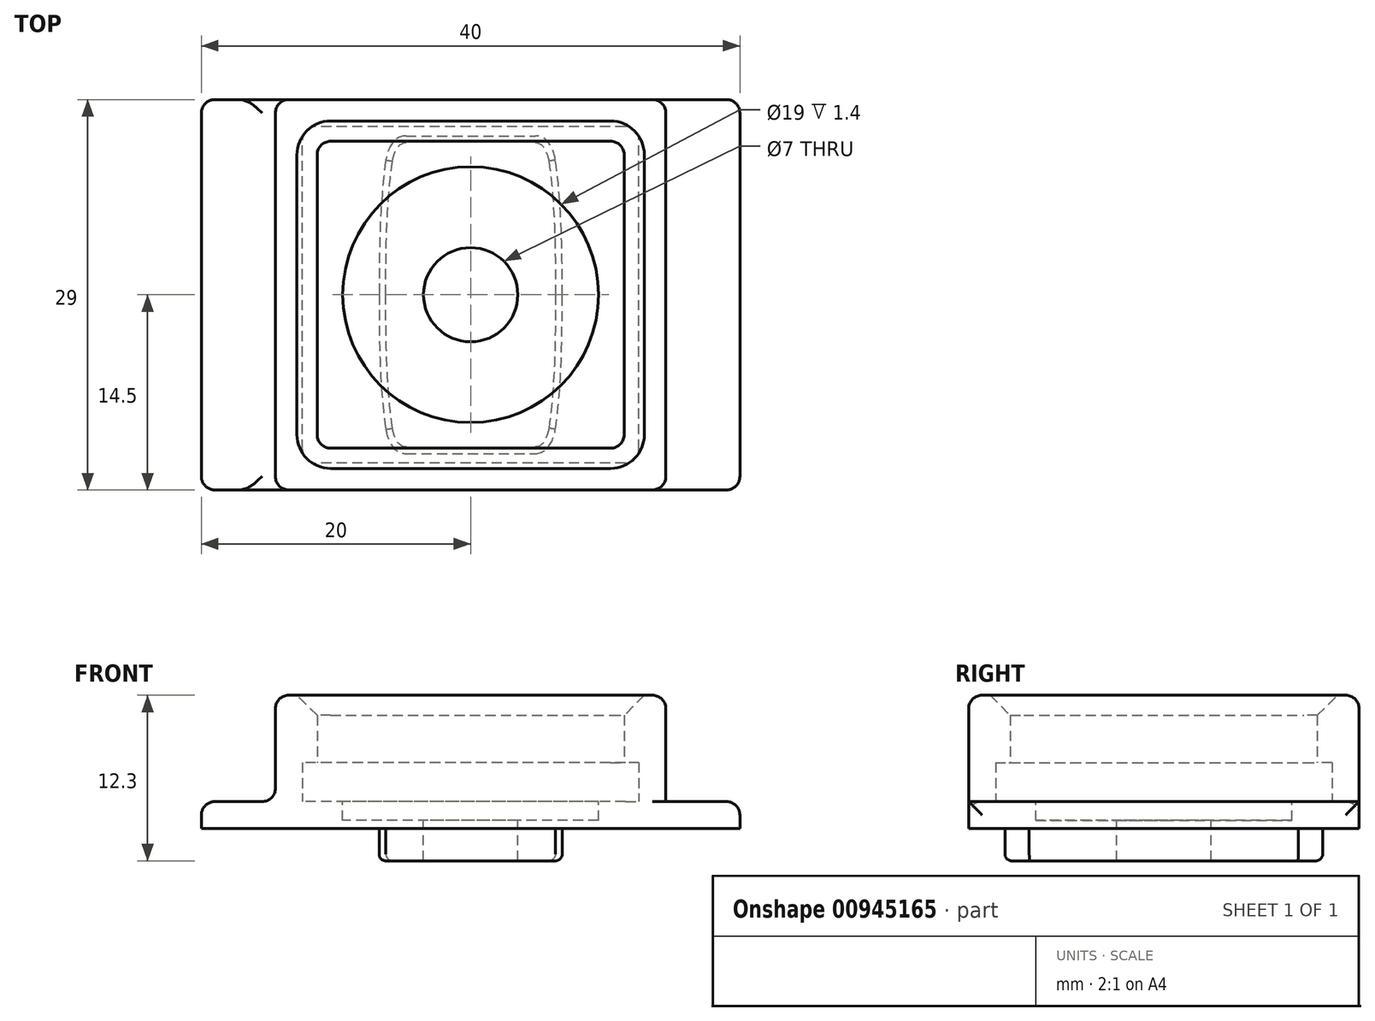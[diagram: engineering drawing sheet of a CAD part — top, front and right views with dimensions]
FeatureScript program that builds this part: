
annotation { "Feature Type Name" : "Feature", "Feature Type Description" : "" }
export const myFeature = defineFeature(function(context is Context, id is Id, definition is map)
    precondition{}
    {
        {
            var Q0;
            Q0=qCreatedBy(makeId("Top.planeOp"),FACE);
            var sketch = newSketch(context, id + "F0", { "sketchPlane" : qUnion([Q0])});
            skLineSegment(sketch, "E0", {"start": v(0, 18.39) * mm, "end": v(0, -21.66) * mm, "construction": true});
            skLineSegment(sketch, "E1", {"start": v(-4.8, 11.8) * mm, "end": v(0, 11.8) * mm});
            skFitSpline(sketch, "E2", {"points": [v(-6.3, 10) * mm, v(-6.8, 0) * mm], "startDerivative": vector(-1.35, -9.46) * mm, "endDerivative": vector(0, -10.27) * mm});
            skFitSpline(sketch, "E3", {"points": [v(-4.8, 11.8) * mm, v(-6.3, 10) * mm], "startDerivative": vector(-2.76, 0) * mm, "endDerivative": vector(-0.47, -2.62) * mm});
            skLineSegment(sketch, "E4.MirrorCS", {"start": v(4.8, 11.8) * mm, "end": v(0, 11.8) * mm});
            skFitSpline(sketch, "E5.MirrorCS", {"points": [v(6.3, 10) * mm, v(6.8, 0) * mm], "startDerivative": vector(1.35, -9.46) * mm, "endDerivative": vector(0, -10.27) * mm});
            skFitSpline(sketch, "E6.MirrorCS", {"points": [v(4.8, 11.8) * mm, v(6.3, 10) * mm], "startDerivative": vector(2.76, 0) * mm, "endDerivative": vector(0.47, -2.62) * mm});
            skLineSegment(sketch, "E7", {"start": v(-11.45, 0) * mm, "end": v(10.17, 0) * mm, "construction": true});
            skFitSpline(sketch, "E8.MirrorCS", {"points": [v(-6.3, -10) * mm, v(-6.8, 0) * mm], "startDerivative": vector(-1.35, 9.46) * mm, "endDerivative": vector(0, 10.27) * mm});
            skFitSpline(sketch, "E9.MirrorCS", {"points": [v(-4.8, -11.8) * mm, v(-6.3, -10) * mm], "startDerivative": vector(-2.76, 0) * mm, "endDerivative": vector(-0.47, 2.62) * mm});
            skLineSegment(sketch, "E10.MirrorCS", {"start": v(-4.8, -11.8) * mm, "end": v(0, -11.8) * mm});
            skLineSegment(sketch, "E11.MirrorCS", {"start": v(4.8, -11.8) * mm, "end": v(0, -11.8) * mm});
            skFitSpline(sketch, "E12.MirrorCS", {"points": [v(4.8, -11.8) * mm, v(6.3, -10) * mm], "startDerivative": vector(2.76, 0) * mm, "endDerivative": vector(0.47, 2.62) * mm});
            skFitSpline(sketch, "E13.MirrorCS", {"points": [v(6.3, -10) * mm, v(6.8, 0) * mm], "startDerivative": vector(1.35, 9.46) * mm, "endDerivative": vector(0, 10.27) * mm});
            skSolve(sketch);
        }
        {
            var Q0;
            Q0 = qSketchRegion(id + "F0", true);
            extrude(context, id + "F1", {"entities" : qUnion([Q0]), "depth" : 2.4 * mm, "offsetDistance" : 25 * mm});
        }
        {
            var Q0;
            Q0=makeQuery(id+"F1.opExtrude","CAP_FACE",FACE,{"disambiguationData":[OSD([sQuery(id+"F0.wireOp",EDGE,"E1"),sQuery(id+"F0.wireOp",EDGE,"E2"),sQuery(id+"F0.wireOp",EDGE,"E3"),sQuery(id+"F0.wireOp",EDGE,"E4.MirrorCS"),sQuery(id+"F0.wireOp",EDGE,"E5.MirrorCS"),sQuery(id+"F0.wireOp",EDGE,"E6.MirrorCS"),sQuery(id+"F0.wireOp",EDGE,"E8.MirrorCS"),sQuery(id+"F0.wireOp",EDGE,"E9.MirrorCS"),sQuery(id+"F0.wireOp",EDGE,"E10.MirrorCS"),sQuery(id+"F0.wireOp",EDGE,"E11.MirrorCS"),sQuery(id+"F0.wireOp",EDGE,"E12.MirrorCS"),sQuery(id+"F0.wireOp",EDGE,"E13.MirrorCS")])],"isStart":false});
            var sketch = newSketch(context, id + "F2", { "sketchPlane" : qUnion([Q0])});
            skLineSegment(sketch, "E14.bottom", {"start": v(-20, 14.5) * mm, "end": v(20, 14.5) * mm});
            skLineSegment(sketch, "E14.top", {"start": v(-20, -14.5) * mm, "end": v(20, -14.5) * mm});
            skLineSegment(sketch, "E14.left", {"start": v(-20, 14.5) * mm, "end": v(-20, -14.5) * mm});
            skLineSegment(sketch, "E14.right", {"start": v(20, 14.5) * mm, "end": v(20, -14.5) * mm});
            skSolve(sketch);
        }
        {
            var Q0;
            Q0 = qSketchRegion(id + "F2", true);
            extrude(context, id + "F3", {"entities" : qUnion([Q0]), "operationType" : NewBodyOperationType.ADD, "depth" : 2 * mm, "offsetDistance" : 25 * mm});
        }
        {
            var Q0;
            Q0=makeQuery(id+"F3.opExtrude","CAP_FACE",FACE,{"disambiguationData":[OSD([sQuery(id+"F2.wireOp",EDGE,"E14.bottom"),sQuery(id+"F2.wireOp",EDGE,"E14.top"),sQuery(id+"F2.wireOp",EDGE,"E14.left"),sQuery(id+"F2.wireOp",EDGE,"E14.right")])],"isStart":false});
            var sketch = newSketch(context, id + "F4", { "sketchPlane" : qUnion([Q0])});
            skCircle(sketch, "E15", {"center": v(0, 0) * mm, "radius": 9.5 * mm});
            skCircle(sketch, "E16", {"center": v(0, 0) * mm, "radius": 3.5 * mm});
            skSolve(sketch);
        }
        {
            var Q0;
            Q0 = qSketchRegion(id + "F4", true);
            extrude(context, id + "F5", {"entities" : qUnion([Q0]), "operationType" : NewBodyOperationType.REMOVE, "oppositeDirection" : true, "depth" : 1.4 * mm, "offsetDistance" : 25 * mm});
        }
        {
            var Q0;
            Q0=makeQuery(id+"F5.boolean.opBoolean","SPLIT",FACE,{"disambiguationData":[TD([makeQuery(id+"F5.opExtrude","SWEPT_FACE",FACE,{"disambiguationData":[OSD([sQuery(id+"F4.wireOp",EDGE,"E16")])]})])],"derivedFrom":makeQuery(id+"F3.opExtrude","CAP_FACE",FACE,{"disambiguationData":[OSD([sQuery(id+"F2.wireOp",EDGE,"E14.bottom"),sQuery(id+"F2.wireOp",EDGE,"E14.top"),sQuery(id+"F2.wireOp",EDGE,"E14.left"),sQuery(id+"F2.wireOp",EDGE,"E14.right")])],"isStart":false})});
            extrude(context, id + "F6", {"entities" : qUnion([Q0]), "operationType" : NewBodyOperationType.REMOVE, "endBound" : BoundingType.THROUGH_ALL, "oppositeDirection" : true, "depth" : 25 * mm, "offsetDistance" : 25 * mm});
        }
        {
            var Q0;
            {var subQ0=sQuery(id+"F2.wireOp",EDGE,"E14.left");var subQ1=sQuery(id+"F2.wireOp",EDGE,"E14.top");var subQ2=sQuery(id+"F2.wireOp",EDGE,"E14.right");var subQ3=sQuery(id+"F2.wireOp",EDGE,"E14.bottom");Q0=makeQuery(id+"F5.boolean.opBoolean","SPLIT",FACE,{"disambiguationData":[TD([makeQuery(id+"F3.opExtrude","SWEPT_FACE",FACE,{"disambiguationData":[OSD([subQ3])]})])],"derivedFrom":makeQuery(id+"F3.opExtrude","CAP_FACE",FACE,{"disambiguationData":[OSD([subQ3,subQ1,subQ0,subQ2])],"isStart":false})});}
            var sketch = newSketch(context, id + "F7", { "sketchPlane" : qUnion([Q0])});
            skLineSegment(sketch, "E17.bottom", {"start": v(12.5, -12.5) * mm, "end": v(-12.5, -12.5) * mm});
            skLineSegment(sketch, "E17.top", {"start": v(12.5, 12.5) * mm, "end": v(-12.5, 12.5) * mm});
            skLineSegment(sketch, "E17.left", {"start": v(12.5, -12.5) * mm, "end": v(12.5, 12.5) * mm});
            skLineSegment(sketch, "E17.right", {"start": v(-12.5, -12.5) * mm, "end": v(-12.5, 12.5) * mm});
            skPoint(sketch, "E17.middle", {"position": v(0, 0) * mm});
            skLineSegment(sketch, "E18.bottom", {"start": v(14.5, -14.5) * mm, "end": v(-14.5, -14.5) * mm});
            skLineSegment(sketch, "E18.top", {"start": v(14.5, 14.5) * mm, "end": v(-14.5, 14.5) * mm});
            skLineSegment(sketch, "E18.left", {"start": v(14.5, -14.5) * mm, "end": v(14.5, 14.5) * mm});
            skLineSegment(sketch, "E18.right", {"start": v(-14.5, -14.5) * mm, "end": v(-14.5, 14.5) * mm});
            skSolve(sketch);
        }
        {
            var Q0;
            Q0 = qSketchRegion(id + "F7", true);
            extrude(context, id + "F8", {"entities" : qUnion([Q0]), "operationType" : NewBodyOperationType.ADD, "depth" : 2.9 * mm, "offsetDistance" : 25 * mm});
        }
        {
            var Q0;
            Q0=makeQuery(id+"F8.opExtrude","CAP_FACE",FACE,{"disambiguationData":[OSD([sQuery(id+"F7.wireOp",EDGE,"E17.bottom"),sQuery(id+"F7.wireOp",EDGE,"E17.top"),sQuery(id+"F7.wireOp",EDGE,"E17.left"),sQuery(id+"F7.wireOp",EDGE,"E17.right"),sQuery(id+"F7.wireOp",EDGE,"E18.bottom"),sQuery(id+"F7.wireOp",EDGE,"E18.top"),sQuery(id+"F7.wireOp",EDGE,"E18.left"),sQuery(id+"F7.wireOp",EDGE,"E18.right")])],"isStart":false});
            var sketch = newSketch(context, id + "F9", { "sketchPlane" : qUnion([Q0])});
            skLineSegment(sketch, "E19.bottom", {"start": v(14.5, -14.5) * mm, "end": v(-14.5, -14.5) * mm});
            skLineSegment(sketch, "E19.top", {"start": v(14.5, 14.5) * mm, "end": v(-14.5, 14.5) * mm});
            skLineSegment(sketch, "E19.left", {"start": v(14.5, -14.5) * mm, "end": v(14.5, 14.5) * mm});
            skLineSegment(sketch, "E19.right", {"start": v(-14.5, -14.5) * mm, "end": v(-14.5, 14.5) * mm});
            skPoint(sketch, "E19.middle", {"position": v(0, 0) * mm});
            skLineSegment(sketch, "E20.bottom", {"start": v(11.4, -11.4) * mm, "end": v(-11.4, -11.4) * mm});
            skLineSegment(sketch, "E20.top", {"start": v(11.4, 11.4) * mm, "end": v(-11.4, 11.4) * mm});
            skLineSegment(sketch, "E20.left", {"start": v(11.4, -11.4) * mm, "end": v(11.4, 11.4) * mm});
            skLineSegment(sketch, "E20.right", {"start": v(-11.4, -11.4) * mm, "end": v(-11.4, 11.4) * mm});
            skSolve(sketch);
        }
        {
            var Q0;
            Q0 = qSketchRegion(id + "F9", true);
            extrude(context, id + "F10", {"entities" : qUnion([Q0]), "operationType" : NewBodyOperationType.ADD, "depth" : 5 * mm, "offsetDistance" : 25 * mm});
        }
        {
            var Q0;
            Q0=makeQuery(id+"F3.opExtrude","SWEPT_EDGE",EDGE,{"disambiguationData":[OSD([sQuery(id+"F2.wireOp",EDGE,"E14.top"),sQuery(id+"F2.wireOp",EDGE,"E14.left")])]});
            var Q1;
            Q1=makeQuery(id+"F3.opExtrude","SWEPT_EDGE",EDGE,{"disambiguationData":[OSD([sQuery(id+"F2.wireOp",EDGE,"E14.top"),sQuery(id+"F2.wireOp",EDGE,"E14.right")])]});
            var Q2;
            Q2=makeQuery(id+"F10.boolean.opBoolean","MERGE",EDGE,{"derivedFrom":[makeQuery(id+"F8.opExtrude","SWEPT_EDGE",EDGE,{"disambiguationData":[OSD([sQuery(id+"F2.wireOp",EDGE,"E14.top"),sQuery(id+"F7.wireOp",EDGE,"E18.bottom"),sQuery(id+"F7.wireOp",EDGE,"E18.left")])]}),makeQuery(id+"F10.opExtrude","SWEPT_EDGE",EDGE,{"disambiguationData":[OSD([sQuery(id+"F9.wireOp",EDGE,"E19.bottom"),sQuery(id+"F9.wireOp",EDGE,"E19.left")])]})]});
            var Q3;
            Q3=makeQuery(id+"F10.boolean.opBoolean","MERGE",EDGE,{"derivedFrom":[makeQuery(id+"F8.opExtrude","SWEPT_EDGE",EDGE,{"disambiguationData":[OSD([sQuery(id+"F2.wireOp",EDGE,"E14.top"),sQuery(id+"F7.wireOp",EDGE,"E18.bottom"),sQuery(id+"F7.wireOp",EDGE,"E18.right")])]}),makeQuery(id+"F10.opExtrude","SWEPT_EDGE",EDGE,{"disambiguationData":[OSD([sQuery(id+"F9.wireOp",EDGE,"E19.bottom"),sQuery(id+"F9.wireOp",EDGE,"E19.right")])]})]});
            var Q4;
            Q4=makeQuery(id+"F8.opExtrude","SWEPT_EDGE",EDGE,{"disambiguationData":[OSD([sQuery(id+"F7.wireOp",EDGE,"E17.bottom"),sQuery(id+"F7.wireOp",EDGE,"E17.left")])]});
            var Q5;
            Q5=makeQuery(id+"F10.opExtrude","SWEPT_EDGE",EDGE,{"disambiguationData":[OSD([sQuery(id+"F9.wireOp",EDGE,"E20.top"),sQuery(id+"F9.wireOp",EDGE,"E20.left")])]});
            var Q6;
            Q6=makeQuery(id+"F8.opExtrude","SWEPT_EDGE",EDGE,{"disambiguationData":[OSD([sQuery(id+"F7.wireOp",EDGE,"E17.top"),sQuery(id+"F7.wireOp",EDGE,"E17.left")])]});
            var Q7;
            Q7=makeQuery(id+"F10.boolean.opBoolean","MERGE",EDGE,{"derivedFrom":[makeQuery(id+"F8.opExtrude","SWEPT_EDGE",EDGE,{"disambiguationData":[OSD([sQuery(id+"F2.wireOp",EDGE,"E14.bottom"),sQuery(id+"F7.wireOp",EDGE,"E18.top"),sQuery(id+"F7.wireOp",EDGE,"E18.right")])]}),makeQuery(id+"F10.opExtrude","SWEPT_EDGE",EDGE,{"disambiguationData":[OSD([sQuery(id+"F9.wireOp",EDGE,"E19.top"),sQuery(id+"F9.wireOp",EDGE,"E19.right")])]})]});
            var Q8;
            Q8=makeQuery(id+"F3.opExtrude","SWEPT_EDGE",EDGE,{"disambiguationData":[OSD([sQuery(id+"F2.wireOp",EDGE,"E14.bottom"),sQuery(id+"F2.wireOp",EDGE,"E14.left")])]});
            var Q9;
            Q9=makeQuery(id+"F3.opExtrude","SWEPT_EDGE",EDGE,{"disambiguationData":[OSD([sQuery(id+"F2.wireOp",EDGE,"E14.bottom"),sQuery(id+"F2.wireOp",EDGE,"E14.right")])]});
            var Q10;
            Q10=makeQuery(id+"F10.boolean.opBoolean","MERGE",EDGE,{"derivedFrom":[makeQuery(id+"F8.opExtrude","SWEPT_EDGE",EDGE,{"disambiguationData":[OSD([sQuery(id+"F2.wireOp",EDGE,"E14.bottom"),sQuery(id+"F7.wireOp",EDGE,"E18.top"),sQuery(id+"F7.wireOp",EDGE,"E18.left")])]}),makeQuery(id+"F10.opExtrude","SWEPT_EDGE",EDGE,{"disambiguationData":[OSD([sQuery(id+"F9.wireOp",EDGE,"E19.top"),sQuery(id+"F9.wireOp",EDGE,"E19.left")])]})]});
            var Q11;
            Q11=makeQuery(id+"F8.opExtrude","SWEPT_EDGE",EDGE,{"disambiguationData":[OSD([sQuery(id+"F7.wireOp",EDGE,"E17.bottom"),sQuery(id+"F7.wireOp",EDGE,"E17.right")])]});
            var Q12;
            Q12=makeQuery(id+"F10.opExtrude","SWEPT_EDGE",EDGE,{"disambiguationData":[OSD([sQuery(id+"F9.wireOp",EDGE,"E20.bottom"),sQuery(id+"F9.wireOp",EDGE,"E20.right")])]});
            var Q13;
            Q13=makeQuery(id+"F8.opExtrude","SWEPT_EDGE",EDGE,{"disambiguationData":[OSD([sQuery(id+"F7.wireOp",EDGE,"E17.top"),sQuery(id+"F7.wireOp",EDGE,"E17.right")])]});
            var Q14;
            Q14=makeQuery(id+"F8.opExtrude","CAP_EDGE",EDGE,{"disambiguationData":[OSD([sQuery(id+"F7.wireOp",EDGE,"E18.left")])],"isStart":true});
            var Q15;
            Q15=makeQuery(id+"F8.opExtrude","CAP_EDGE",EDGE,{"disambiguationData":[OSD([sQuery(id+"F7.wireOp",EDGE,"E18.right")])],"isStart":true});
            var Q16;
            Q16=makeQuery(id+"F3.opExtrude","CAP_EDGE",EDGE,{"disambiguationData":[OSD([sQuery(id+"F2.wireOp",EDGE,"E14.left")])],"isStart":false});
            var Q17;
            Q17=makeQuery(id+"F3.opExtrude","CAP_EDGE",EDGE,{"disambiguationData":[OSD([sQuery(id+"F2.wireOp",EDGE,"E14.right")])],"isStart":false});
            var Q18;
            Q18=makeQuery(id+"F10.opExtrude","CAP_EDGE",EDGE,{"disambiguationData":[OSD([sQuery(id+"F9.wireOp",EDGE,"E19.left")])],"isStart":false});
            var Q19;
            Q19=makeQuery(id+"F10.opExtrude","CAP_EDGE",EDGE,{"disambiguationData":[OSD([sQuery(id+"F9.wireOp",EDGE,"E19.bottom")])],"isStart":false});
            var Q20;
            Q20=makeQuery(id+"F10.opExtrude","CAP_EDGE",EDGE,{"disambiguationData":[OSD([sQuery(id+"F9.wireOp",EDGE,"E19.right")])],"isStart":false});
            var Q21;
            Q21=makeQuery(id+"F10.opExtrude","CAP_EDGE",EDGE,{"disambiguationData":[OSD([sQuery(id+"F9.wireOp",EDGE,"E19.top")])],"isStart":false});
            var Q22;
            Q22=makeQuery(id+"F10.opExtrude","SWEPT_EDGE",EDGE,{"disambiguationData":[OSD([sQuery(id+"F9.wireOp",EDGE,"E20.bottom"),sQuery(id+"F9.wireOp",EDGE,"E20.left")])]});
            var Q23;
            Q23=makeQuery(id+"F10.opExtrude","SWEPT_EDGE",EDGE,{"disambiguationData":[OSD([sQuery(id+"F9.wireOp",EDGE,"E20.top"),sQuery(id+"F9.wireOp",EDGE,"E20.right")])]});
            fillet(context, id + "F11", {"entities" : qUnion([Q0, Q1, Q2, Q3, Q4, Q5, Q6, Q7, Q8, Q9, Q10, Q11, Q12, Q13, Q14, Q15, Q16, Q17, Q18, Q19, Q20, Q21, Q22, Q23]), "radius" : 1 * mm, "tangentPropagation" : true, "allowEdgeOverflow" : false});
        }
        {
            var Q0;
            Q0=makeQuery(id+"F10.opExtrude","CAP_EDGE",EDGE,{"disambiguationData":[OSD([sQuery(id+"F9.wireOp",EDGE,"E20.top")])],"isStart":false});
            chamfer(context, id + "F12", {"entities" : qUnion([Q0]), "width" : 1.5 * mm, "tangentPropagation" : true});
        }
        {
            var Q0;
            Q0=makeQuery(id+"F1.opExtrude","CAP_EDGE",EDGE,{"disambiguationData":[OSD([sQuery(id+"F0.wireOp",EDGE,"E8.MirrorCS")])],"isStart":true});
            var Q1;
            Q1=makeQuery(id+"F1.opExtrude","CAP_EDGE",EDGE,{"disambiguationData":[OSD([sQuery(id+"F0.wireOp",EDGE,"E10.MirrorCS"),sQuery(id+"F0.wireOp",EDGE,"E11.MirrorCS")])],"isStart":true});
            var Q2;
            Q2=makeQuery(id+"F1.opExtrude","CAP_EDGE",EDGE,{"disambiguationData":[OSD([sQuery(id+"F0.wireOp",EDGE,"E1"),sQuery(id+"F0.wireOp",EDGE,"E4.MirrorCS")])],"isStart":true});
            var Q3;
            Q3=makeQuery(id+"F1.opExtrude","CAP_EDGE",EDGE,{"disambiguationData":[OSD([sQuery(id+"F0.wireOp",EDGE,"E5.MirrorCS")])],"isStart":true});
            fillet(context, id + "F13", {"entities" : qUnion([Q0, Q1, Q2, Q3]), "radius" : 0.5 * mm, "tangentPropagation" : true, "allowEdgeOverflow" : false});
        }
    });
